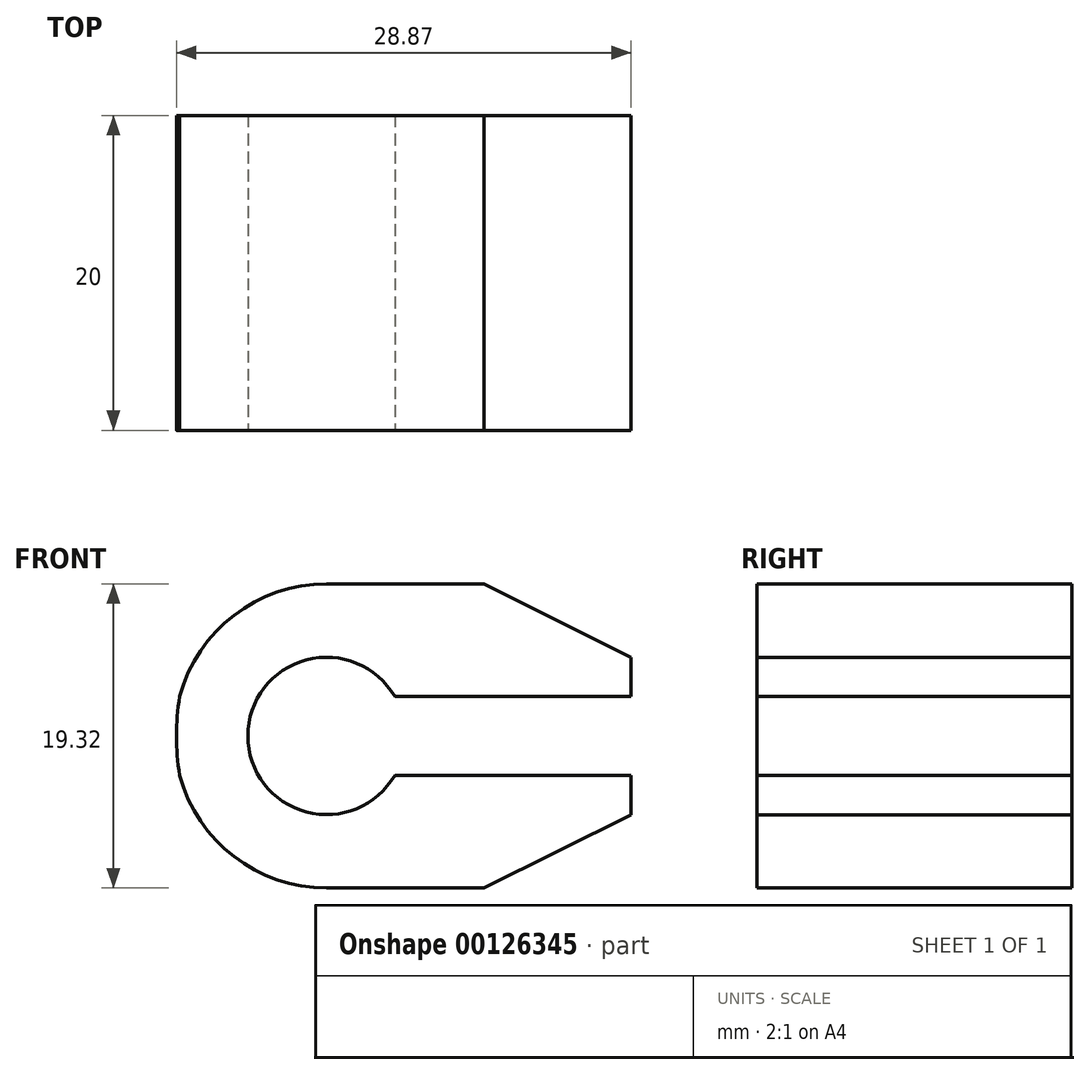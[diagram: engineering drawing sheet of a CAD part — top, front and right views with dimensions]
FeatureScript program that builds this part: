
annotation { "Feature Type Name" : "Feature", "Feature Type Description" : "" }
export const myFeature = defineFeature(function(context is Context, id is Id, definition is map)
    precondition{}
    {
        {
            var Q0;
            Q0=qCreatedBy(makeId("Front.planeOp"),FACE);
            var sketch = newSketch(context, id + "F0", { "sketchPlane" : qUnion([Q0])});
            skLineSegment(sketch, "E0", {"start": v(22.2, 0) * mm, "end": v(-26.08, 0) * mm, "construction": true});
            skArc(sketch, "E1", {"start": v(5, 0) * mm, "mid": v(0, 5) * mm, "end": v(-5, 0) * mm});
            skLineSegment(sketch, "E2", {"start": v(-4.33, 2.5) * mm, "end": v(-9.33, 2.5) * mm});
            skLineSegment(sketch, "E3", {"start": v(4.33, 2.5) * mm, "end": v(19.33, 2.5) * mm});
            skLineSegment(sketch, "E4", {"start": v(0, 9.66) * mm, "end": v(10, 9.66) * mm});
            skLineSegment(sketch, "E5", {"start": v(10, 9.66) * mm, "end": v(19.33, 5) * mm});
            skLineSegment(sketch, "E6", {"start": v(19.33, 5) * mm, "end": v(19.33, 2.5) * mm});
            skArc(sketch, "E7", {"start": v(0, 9.66) * mm, "mid": v(-5.88, 7.66) * mm, "end": v(-9.33, 2.5) * mm});
            skLineSegment(sketch, "E8", {"start": v(19.33, 2.5) * mm, "end": v(19.33, 0) * mm});
            skArc(sketch, "E9.MirrorCS", {"start": v(0, -9.66) * mm, "mid": v(-5.88, -7.66) * mm, "end": v(-9.33, -2.5) * mm});
            skArc(sketch, "E10.MirrorCS", {"start": v(5, 0) * mm, "mid": v(0, -5) * mm, "end": v(-5, 0) * mm});
            skLineSegment(sketch, "E11.MirrorCS", {"start": v(0, -9.66) * mm, "end": v(10, -9.66) * mm});
            skLineSegment(sketch, "E12.MirrorCS", {"start": v(4.33, -2.5) * mm, "end": v(19.33, -2.5) * mm});
            skLineSegment(sketch, "E13.MirrorCS", {"start": v(19.33, -5) * mm, "end": v(19.33, -2.5) * mm});
            skLineSegment(sketch, "E14.MirrorCS", {"start": v(10, -9.66) * mm, "end": v(19.33, -5) * mm});
            skLineSegment(sketch, "E15.MirrorCS", {"start": v(19.33, -2.5) * mm, "end": v(19.33, 0) * mm});
            skArc(sketch, "E16", {"start": v(-9.33, 2.5) * mm, "mid": v(-9.54, 0) * mm, "end": v(-9.33, -2.5) * mm});
            skSolve(sketch);
        }
        {
            var Q0;
            {var subQ1=sQuery(id+"F0.wireOp",EDGE,"E2");Q0=makeQuery(id+"F0.imprint","IMPRINT",FACE,{"disambiguationData":[TD([[makeQuery(id+"F0.imprint","IMPRINT",EDGE,{"derivedFrom":subQ1}),-1.0]])]});}
            var Q1;
            {var subQ4=sQuery(id+"F0.wireOp",EDGE,"E2");Q1=makeQuery(id+"F0.imprint","IMPRINT",FACE,{"disambiguationData":[TD([[makeQuery(id+"F0.imprint","IMPRINT",EDGE,{"derivedFrom":subQ4}),1.0]])]});}
            extrude(context, id + "F1", {"entities" : qUnion([Q0, Q1]), "oppositeDirection" : true, "depth" : 20 * mm});
        }
    });
